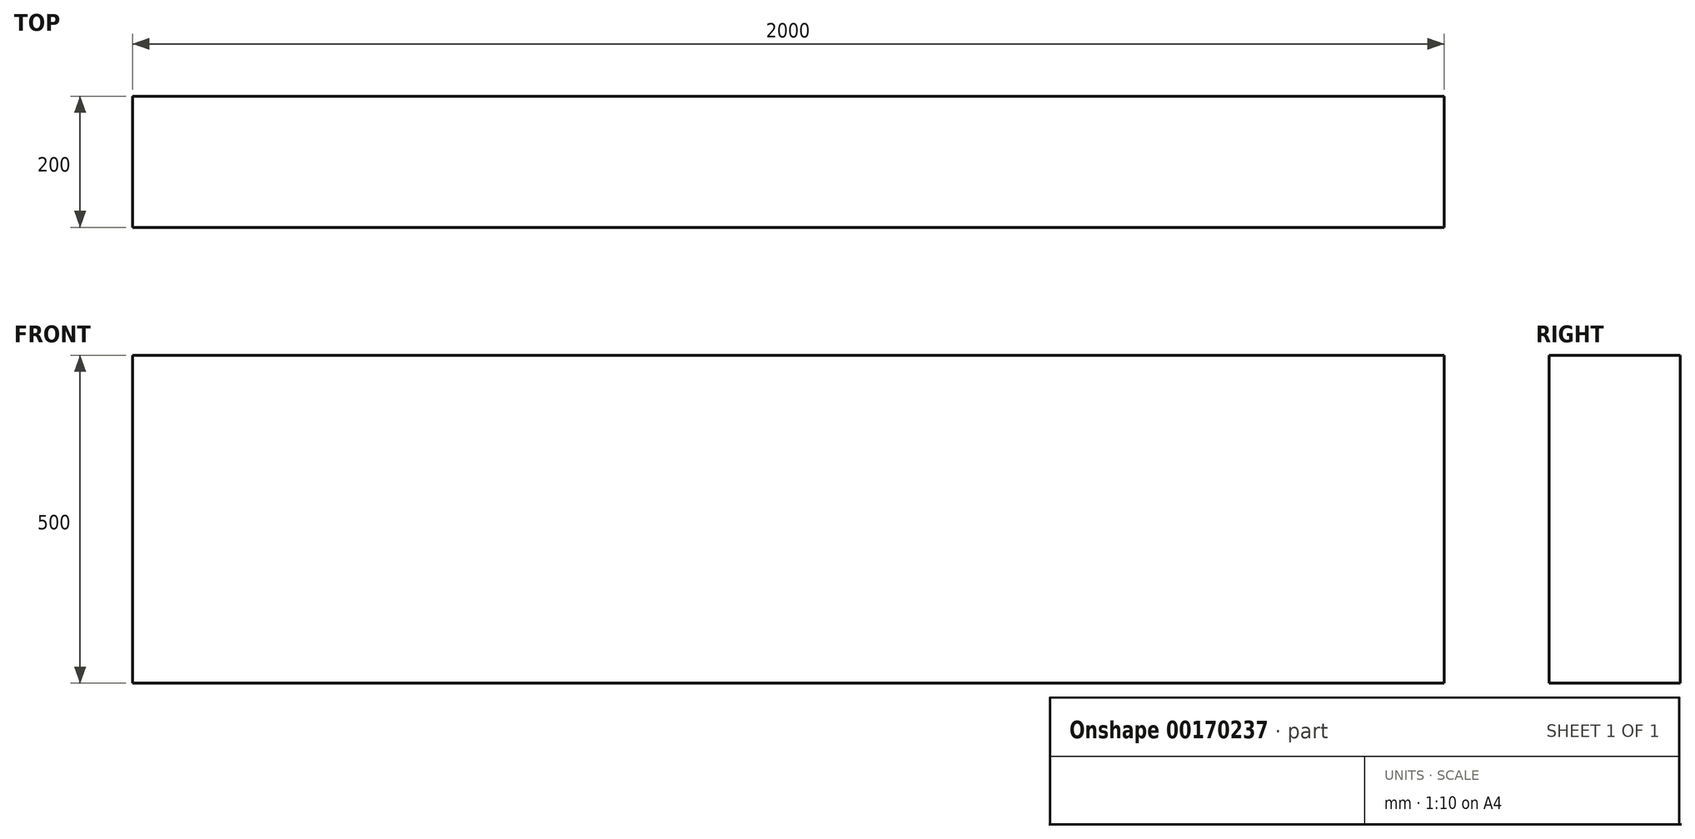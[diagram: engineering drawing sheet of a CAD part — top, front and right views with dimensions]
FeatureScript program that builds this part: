
annotation { "Feature Type Name" : "Feature", "Feature Type Description" : "" }
export const myFeature = defineFeature(function(context is Context, id is Id, definition is map)
    precondition{}
    {
        {
            var Q0;
            Q0=qCreatedBy(makeId("Front.planeOp"),FACE);
            var sketch = newSketch(context, id + "F0", { "sketchPlane" : qUnion([Q0])});
            skLineSegment(sketch, "E0.bottom", {"start": v(0, 0) * mm, "end": v(-2000, 0) * mm});
            skLineSegment(sketch, "E0.top", {"start": v(0, -500) * mm, "end": v(-2000, -500) * mm});
            skLineSegment(sketch, "E0.left", {"start": v(0, 0) * mm, "end": v(0, -500) * mm});
            skLineSegment(sketch, "E0.right", {"start": v(-2000, 0) * mm, "end": v(-2000, -500) * mm});
            skSolve(sketch);
        }
        {
            var Q0;
            Q0=makeQuery(id+"F0.imprint","IMPRINT",FACE,{"disambiguationData":[TD([[makeQuery(id+"F0.imprint","IMPRINT",EDGE,{"derivedFrom":sQuery(id+"F0.wireOp",EDGE,"E0.bottom")}),1.0]])]});
            extrude(context, id + "F1", {"entities" : qUnion([Q0]), "depth" : 200 * mm});
        }
    });
